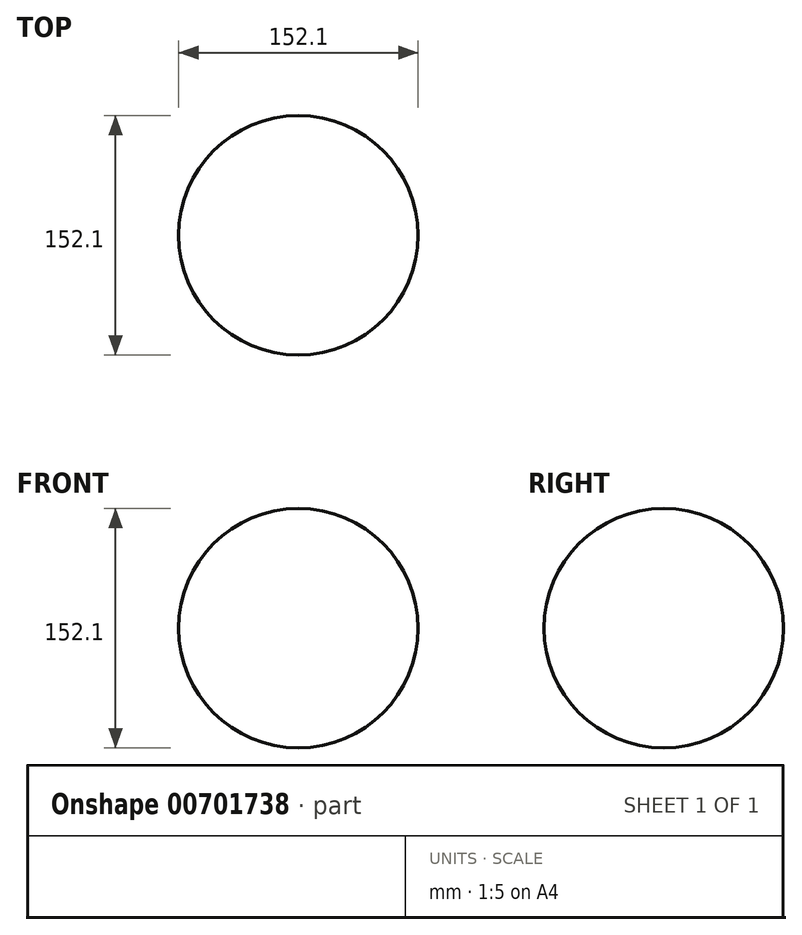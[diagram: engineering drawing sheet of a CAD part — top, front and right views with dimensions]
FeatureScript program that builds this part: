
annotation { "Feature Type Name" : "Feature", "Feature Type Description" : "" }
export const myFeature = defineFeature(function(context is Context, id is Id, definition is map)
    precondition{}
    {
        {
            var Q0;
            Q0=qCreatedBy(makeId("Front.planeOp"),FACE);
            var sketch = newSketch(context, id + "F0", { "sketchPlane" : qUnion([Q0])});
            skArc(sketch, "E0", {"start": v(76.05, 0) * mm, "mid": v(0, 76.05) * mm, "end": v(-76.05, 0) * mm});
            skLineSegment(sketch, "E1", {"start": v(-76.05, 0) * mm, "end": v(76.05, 0) * mm});
            skSolve(sketch);
        }
        {
            var Q0;
            Q0=sQuery(id+"F0.wireOp",EDGE,"E0");
            var Q1;
            Q1=sQuery(id+"F0.wireOp",EDGE,"E1");
            revolve(context, id + "F1", {"bodyType" : ToolBodyType.SURFACE, "surfaceOperationType" : NewSurfaceOperationType.NEW, "surfaceEntities" : qUnion([Q0]), "axis" : qUnion([Q1]), "revolveType" : RevolveType.FULL});
        }
    });
